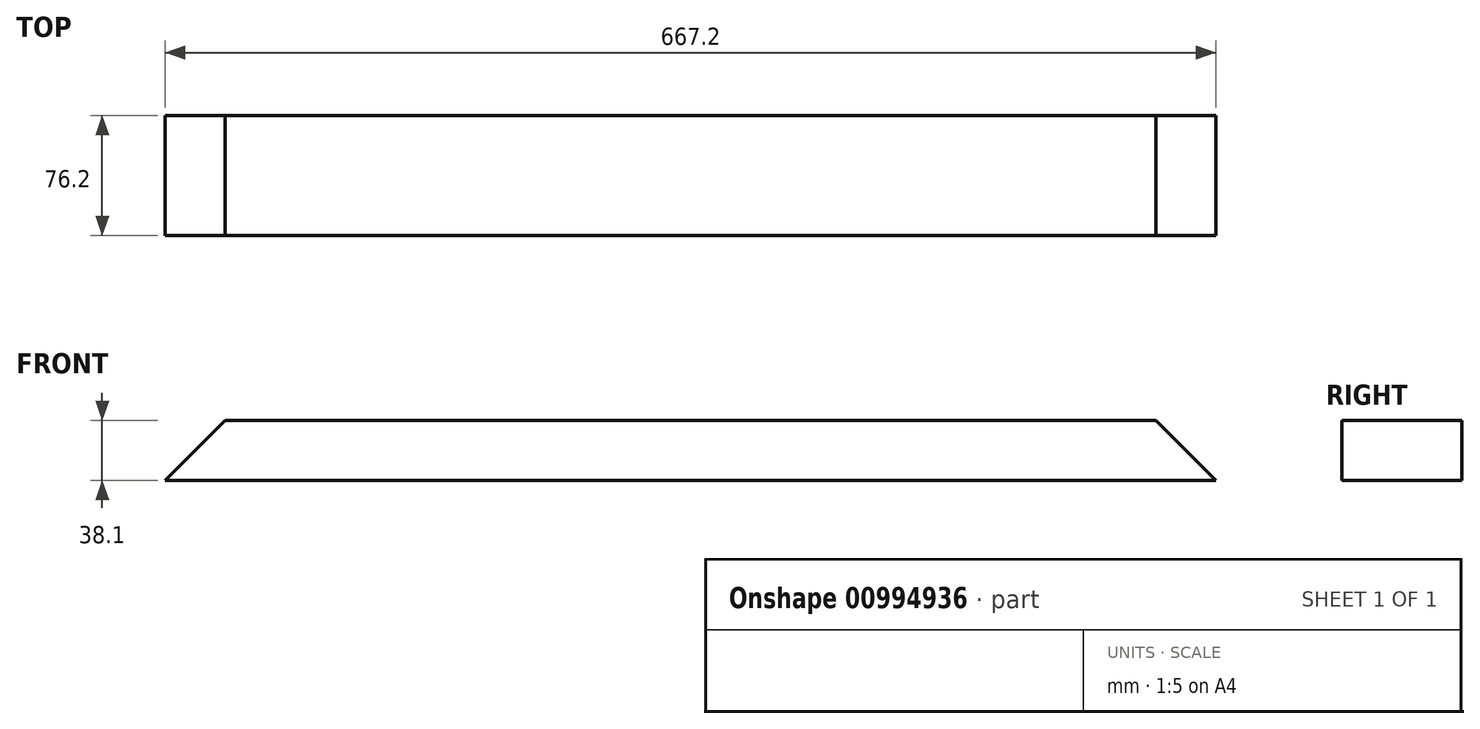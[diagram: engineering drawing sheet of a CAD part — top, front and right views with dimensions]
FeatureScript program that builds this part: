
annotation { "Feature Type Name" : "Feature", "Feature Type Description" : "" }
export const myFeature = defineFeature(function(context is Context, id is Id, definition is map)
    precondition{}
    {
        {
            var Q0;
            Q0=qCreatedBy(makeId("Front.planeOp"),FACE);
            var sketch = newSketch(context, id + "F0", { "sketchPlane" : qUnion([Q0])});
            skLineSegment(sketch, "E0", {"start": v(-333.6, 0) * mm, "end": v(333.6, 0) * mm});
            skLineSegment(sketch, "E1", {"start": v(333.6, 0) * mm, "end": v(295.5, 38.1) * mm});
            skLineSegment(sketch, "E2", {"start": v(295.5, 38.1) * mm, "end": v(-295.5, 38.1) * mm});
            skLineSegment(sketch, "E3", {"start": v(-295.5, 38.1) * mm, "end": v(-333.6, 0) * mm});
            skSolve(sketch);
        }
        {
            var Q0;
            Q0 = qSketchRegion(id + "F0", true);
            extrude(context, id + "F1", {"entities" : qUnion([Q0]), "oppositeDirection" : true, "depth" : 76.2 * mm, "offsetDistance" : 25.4 * mm});
        }
    });
